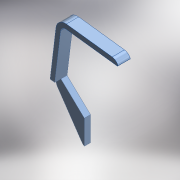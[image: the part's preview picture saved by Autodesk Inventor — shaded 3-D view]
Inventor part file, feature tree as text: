
AUTODESK INVENTOR PART (.ipt)
format: ipt  version: 2018 (Build 220112000, 112)  size: 168,448 bytes
history: native  units: in
note: dims shown in document units (in); Inventor stores cm internally (conversion verified against a paired STEP export)
features: fillet x3, extrude x2, other x1
ambient origin geometry x8: Origin, YZ Plane, XZ Plane, XY Plane, X Axis, Y Axis, Z Axis, Center Point
bodies: Body1 (feature_tree)
feature tree (6):
  other  "Base Sketch"
  extrude  "Lower Arm"  Depth=0.8661in
  extrude  "Upper Arm"  Depth=0.2067in
  fillet  "Fillet1"  [1 undecoded]
  fillet  "Fillet3"  Radius=0.4134in
  fillet  "Fillet4"  [1 undecoded]
note: 2 required parameter values undecoded (feature->parameter linkage not recoverable at this tier; creation-order binding heuristic only, values carry confidence <= 0.55)
